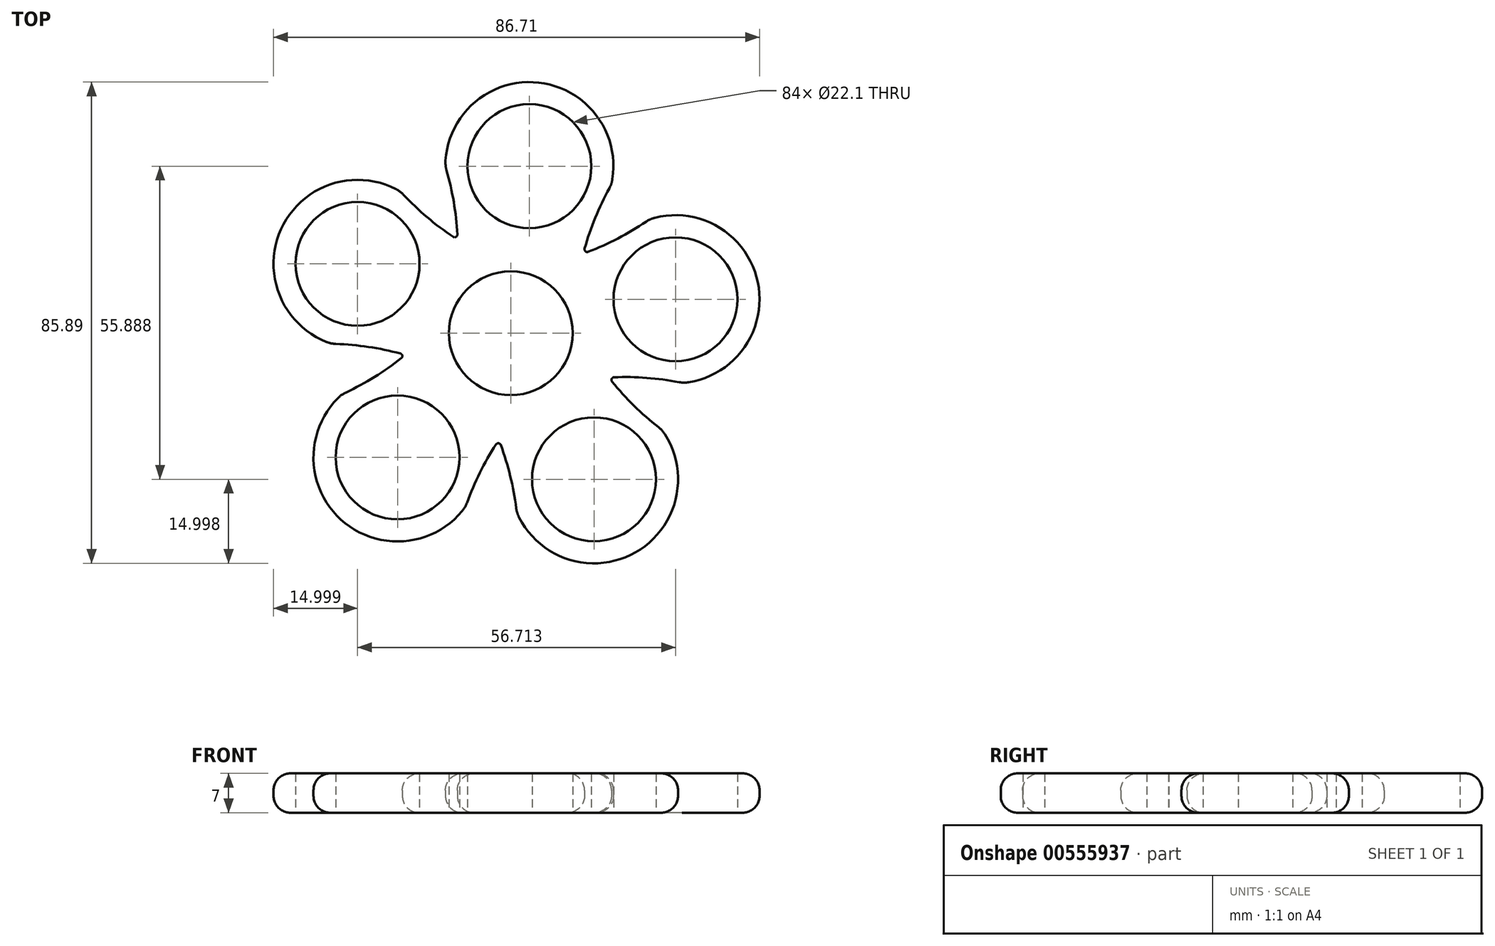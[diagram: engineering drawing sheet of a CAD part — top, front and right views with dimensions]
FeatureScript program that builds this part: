
annotation { "Feature Type Name" : "Feature", "Feature Type Description" : "" }
export const myFeature = defineFeature(function(context is Context, id is Id, definition is map)
    precondition{}
    {
        {
            var Q0;
            Q0=qCreatedBy(makeId("Top.planeOp"),FACE);
            var sketch = newSketch(context, id + "F0", { "sketchPlane" : qUnion([Q0])});
            skCircle(sketch, "E0.cCircle", {"center": v(0, 0) * mm, "radius": 24.27 * mm, "construction": true});
            skPoint(sketch, "E0.0.midPoint", {"position": v(-12, 21.1) * mm});
            skCircle(sketch, "E1", {"center": v(3.32, 29.82) * mm, "radius": 11.05 * mm});
            skCircle(sketch, "E2", {"center": v(0, 0) * mm, "radius": 11.05 * mm});
            skCircle(sketch, "E3", {"center": v(-27.33, 12.37) * mm, "radius": 11.05 * mm});
            skCircle(sketch, "E4", {"center": v(-20.2, -22.17) * mm, "radius": 11.05 * mm});
            skCircle(sketch, "E5", {"center": v(14.84, -26.07) * mm, "radius": 11.05 * mm});
            skCircle(sketch, "E6", {"center": v(29.38, 6.06) * mm, "radius": 11.05 * mm});
            skArc(sketch, "E7", {"start": v(-11.65, 30.79) * mm, "mid": v(3.8, 44.8) * mm, "end": v(18.32, 29.82) * mm});
            skLineSegment(sketch, "E8", {"start": v(3.32, 29.82) * mm, "end": v(-11.68, 29.82) * mm});
            skLineSegment(sketch, "E9", {"start": v(3.32, 29.82) * mm, "end": v(18.32, 29.82) * mm});
            skCircle(sketch, "E10", {"center": v(0, 0) * mm, "radius": 15 * mm});
            skArc(sketch, "E11", {"start": v(-9.54, 17.62) * mm, "mid": v(-10.18, 23.4) * mm, "end": v(-11.47, 29.09) * mm});
            skPoint(sketch, "E12.visualSharp", {"position": v(-11.68, 29.82) * mm});
            skArc(sketch, "E12.filletArc", {"start": v(-11.65, 30.79) * mm, "mid": v(-11.63, 29.93) * mm, "end": v(-11.47, 29.09) * mm});
            skLineSegment(sketch, "E13", {"start": v(0, 0) * mm, "end": v(3.32, 29.82) * mm});
            skLineSegment(sketch, "E14", {"start": v(0, 0) * mm, "end": v(29.38, 6.06) * mm});
            skArc(sketch, "E15.MirrorCS", {"start": v(18.13, 27.47) * mm, "mid": v(6.14, 44.55) * mm, "end": v(-11.31, 33.11) * mm});
            skArc(sketch, "E16.MirrorCS", {"start": v(13.18, 15.09) * mm, "mid": v(15.08, 20.6) * mm, "end": v(17.58, 25.85) * mm});
            skArc(sketch, "E17.MirrorCS", {"start": v(18.13, 27.47) * mm, "mid": v(17.93, 26.64) * mm, "end": v(17.58, 25.85) * mm});
            skArc(sketch, "E18.MirrorCS", {"start": v(18.07, -8.65) * mm, "mid": v(22, -12.95) * mm, "end": v(26.37, -16.8) * mm});
            skArc(sketch, "E19.MirrorCS", {"start": v(-1.8, -19.95) * mm, "mid": v(-0.1, -25.52) * mm, "end": v(0.97, -31.25) * mm});
            skArc(sketch, "E20.MirrorCS", {"start": v(1.48, -32.89) * mm, "mid": v(21.22, -39.65) * mm, "end": v(28.62, -20.14) * mm});
            skArc(sketch, "E21.MirrorCS", {"start": v(1.48, -32.89) * mm, "mid": v(1.16, -32.1) * mm, "end": v(0.97, -31.25) * mm});
            skArc(sketch, "E22.MirrorCS", {"start": v(27.52, -18.06) * mm, "mid": v(27, -17.38) * mm, "end": v(26.37, -16.8) * mm});
            skArc(sketch, "E23.MirrorCS", {"start": v(27.52, -18.06) * mm, "mid": v(23.26, -38.49) * mm, "end": v(2.7, -34.89) * mm});
            skArc(sketch, "E24.MirrorCS", {"start": v(-19.53, -4.46) * mm, "mid": v(-24.3, -7.8) * mm, "end": v(-29.42, -10.58) * mm});
            skArc(sketch, "E25.MirrorCS", {"start": v(-2.64, -19.86) * mm, "mid": v(-5.52, -24.92) * mm, "end": v(-7.82, -30.27) * mm});
            skArc(sketch, "E26.MirrorCS", {"start": v(-8.67, -31.76) * mm, "mid": v(-29.42, -34.01) * mm, "end": v(-32.35, -13.35) * mm});
            skArc(sketch, "E27.MirrorCS", {"start": v(-8.67, -31.76) * mm, "mid": v(-8.18, -31.05) * mm, "end": v(-7.82, -30.27) * mm});
            skArc(sketch, "E28.MirrorCS", {"start": v(-30.82, -11.57) * mm, "mid": v(-30.16, -11.02) * mm, "end": v(-29.42, -10.58) * mm});
            skArc(sketch, "E29.MirrorCS", {"start": v(-30.82, -11.57) * mm, "mid": v(-31.15, -32.43) * mm, "end": v(-10.3, -33.44) * mm});
            skArc(sketch, "E30.MirrorCS", {"start": v(11.87, 9.17) * mm, "mid": v(14.01, 17.76) * mm, "end": v(17.58, 25.85) * mm});
            skArc(sketch, "E31.MirrorCS", {"start": v(-9.56, 11.56) * mm, "mid": v(-9.76, 20.4) * mm, "end": v(-11.47, 29.09) * mm});
            skArc(sketch, "E32.MirrorCS", {"start": v(-13.95, -5.52) * mm, "mid": v(-22.42, -2.98) * mm, "end": v(-31.2, -1.92) * mm});
            skArc(sketch, "E33.MirrorCS", {"start": v(-10.28, 17.2) * mm, "mid": v(-14.93, 20.7) * mm, "end": v(-19.16, 24.71) * mm});
            skArc(sketch, "E34.MirrorCS", {"start": v(-19.7, -3.63) * mm, "mid": v(-25.4, -2.45) * mm, "end": v(-31.2, -1.92) * mm});
            skArc(sketch, "E35.MirrorCS", {"start": v(-32.88, -1.57) * mm, "mid": v(-41.44, 17.47) * mm, "end": v(-22.7, 26.64) * mm});
            skArc(sketch, "E36.MirrorCS", {"start": v(-20.53, 25.74) * mm, "mid": v(-40.47, 19.6) * mm, "end": v(-34.99, -0.53) * mm});
            skArc(sketch, "E37.MirrorCS", {"start": v(-20.53, 25.74) * mm, "mid": v(-19.8, 25.28) * mm, "end": v(-19.16, 24.71) * mm});
            skArc(sketch, "E38.MirrorCS", {"start": v(-32.88, -1.57) * mm, "mid": v(-32.06, -1.81) * mm, "end": v(-31.2, -1.92) * mm});
            skArc(sketch, "E39.MirrorCS", {"start": v(13.8, 14.52) * mm, "mid": v(19.12, 16.91) * mm, "end": v(24.12, 19.9) * mm});
            skArc(sketch, "E40.MirrorCS", {"start": v(18.42, -7.87) * mm, "mid": v(24.25, -7.97) * mm, "end": v(30.02, -8.73) * mm});
            skArc(sketch, "E41.MirrorCS", {"start": v(31.73, -8.76) * mm, "mid": v(44.27, 7.93) * mm, "end": v(28, 21) * mm});
            skArc(sketch, "E42.MirrorCS", {"start": v(31.73, -8.76) * mm, "mid": v(30.88, -8.82) * mm, "end": v(30.02, -8.73) * mm});
            skArc(sketch, "E43.MirrorCS", {"start": v(25.68, 20.6) * mm, "mid": v(43.8, 10.23) * mm, "end": v(34.02, -8.2) * mm});
            skArc(sketch, "E44.MirrorCS", {"start": v(25.68, 20.6) * mm, "mid": v(24.87, 20.31) * mm, "end": v(24.12, 19.9) * mm});
            skPoint(sketch, "E45.newPointA", {"position": v(-5.05, 14.12) * mm});
            skPoint(sketch, "E45.newPointB", {"position": v(-9.56, 11.56) * mm});
            skArc(sketch, "E45.filletArc", {"start": v(-10.28, 17.2) * mm, "mid": v(-9.78, 17.18) * mm, "end": v(-9.54, 17.62) * mm});
            skPoint(sketch, "E46.newPointA", {"position": v(-15, -0.44) * mm});
            skPoint(sketch, "E46.newPointB", {"position": v(-13.95, -5.52) * mm});
            skArc(sketch, "E46.filletArc", {"start": v(-19.53, -4.46) * mm, "mid": v(-19.36, -4) * mm, "end": v(-19.7, -3.63) * mm});
            skPoint(sketch, "E47.newPointA", {"position": v(0.95, -14.97) * mm});
            skPoint(sketch, "E47.newPointB", {"position": v(-4.21, -14.4) * mm});
            skArc(sketch, "E47.filletArc", {"start": v(-1.8, -19.95) * mm, "mid": v(-2.19, -19.64) * mm, "end": v(-2.64, -19.86) * mm});
            skPoint(sketch, "E48.newPointA", {"position": v(14.53, -3.73) * mm});
            skPoint(sketch, "E48.newPointB", {"position": v(12.39, -8.46) * mm});
            skArc(sketch, "E48.filletArc", {"start": v(18.42, -7.87) * mm, "mid": v(18, -8.15) * mm, "end": v(18.07, -8.65) * mm});
            skPoint(sketch, "E49.newPointA", {"position": v(8.03, 12.67) * mm});
            skPoint(sketch, "E49.newPointB", {"position": v(11.87, 9.17) * mm});
            skArc(sketch, "E49.filletArc", {"start": v(13.18, 15.09) * mm, "mid": v(13.32, 14.6) * mm, "end": v(13.8, 14.52) * mm});
            skSolve(sketch);
        }
        {
            var Q0;
            Q0=qSketchRegion(id+"F0",true);
            var Q1;
            {var subQ5=sQuery(id+"F0.wireOp",EDGE,"E13");var subQ7=sQuery(id+"F0.wireOp",EDGE,"E2");var subQ8=makeQuery(id+"F0.imprint","INTERSECT",VERTEX,{"derivedFrom":[subQ7,subQ5]});Q1=makeQuery(id+"F0.imprint","IMPRINT",FACE,{"disambiguationData":[TD([[makeQuery(id+"F0.imprint","IMPRINT",EDGE,{"disambiguationData":[TD([[subQ8,-1.0]])],"derivedFrom":subQ7}),-1.0]])]});}
            var Q2;
            {var subQ0=sQuery(id+"F0.wireOp",EDGE,"E13");var subQ1=sQuery(id+"F0.wireOp",EDGE,"E2");var subQ2=makeQuery(id+"F0.imprint","INTERSECT",VERTEX,{"derivedFrom":[subQ1,subQ0]});Q2=makeQuery(id+"F0.imprint","IMPRINT",FACE,{"disambiguationData":[TD([[makeQuery(id+"F0.imprint","IMPRINT",EDGE,{"disambiguationData":[TD([[subQ2,1.0]])],"derivedFrom":subQ1}),-1.0]])]});}
            extrude(context, id + "F1", {"entities" : qUnion([Q0, Q1, Q2]), "depth" : 7 * mm});
        }
        {
            var Q0;
            Q0=makeQuery(id+"F1.opExtrude","CAP_EDGE",EDGE,{"disambiguationData":[OSD([sQuery(id+"F0.wireOp",EDGE,"E7"),sQuery(id+"F0.wireOp",EDGE,"E15.MirrorCS")])],"isStart":false});
            var Q1;
            Q1=makeQuery(id+"F1.opExtrude","CAP_EDGE",EDGE,{"disambiguationData":[OSD([sQuery(id+"F0.wireOp",EDGE,"E35.MirrorCS"),sQuery(id+"F0.wireOp",EDGE,"E36.MirrorCS")])],"isStart":false});
            fillet(context, id + "F2", {"entities" : qUnion([Q0, Q1]), "radius" : 3 * mm, "tangentPropagation" : true, "allowEdgeOverflow" : false});
        }
        {
            var Q0;
            Q0=makeQuery(id+"F1.opExtrude","CAP_EDGE",EDGE,{"disambiguationData":[OSD([sQuery(id+"F0.wireOp",EDGE,"E35.MirrorCS"),sQuery(id+"F0.wireOp",EDGE,"E36.MirrorCS")])],"isStart":true});
            var Q1;
            Q1=makeQuery(id+"F1.opExtrude","CAP_EDGE",EDGE,{"disambiguationData":[OSD([sQuery(id+"F0.wireOp",EDGE,"E26.MirrorCS"),sQuery(id+"F0.wireOp",EDGE,"E29.MirrorCS")])],"isStart":true});
            fillet(context, id + "F3", {"entities" : qUnion([Q0, Q1]), "radius" : 3 * mm, "tangentPropagation" : true, "allowEdgeOverflow" : false});
        }
    });
